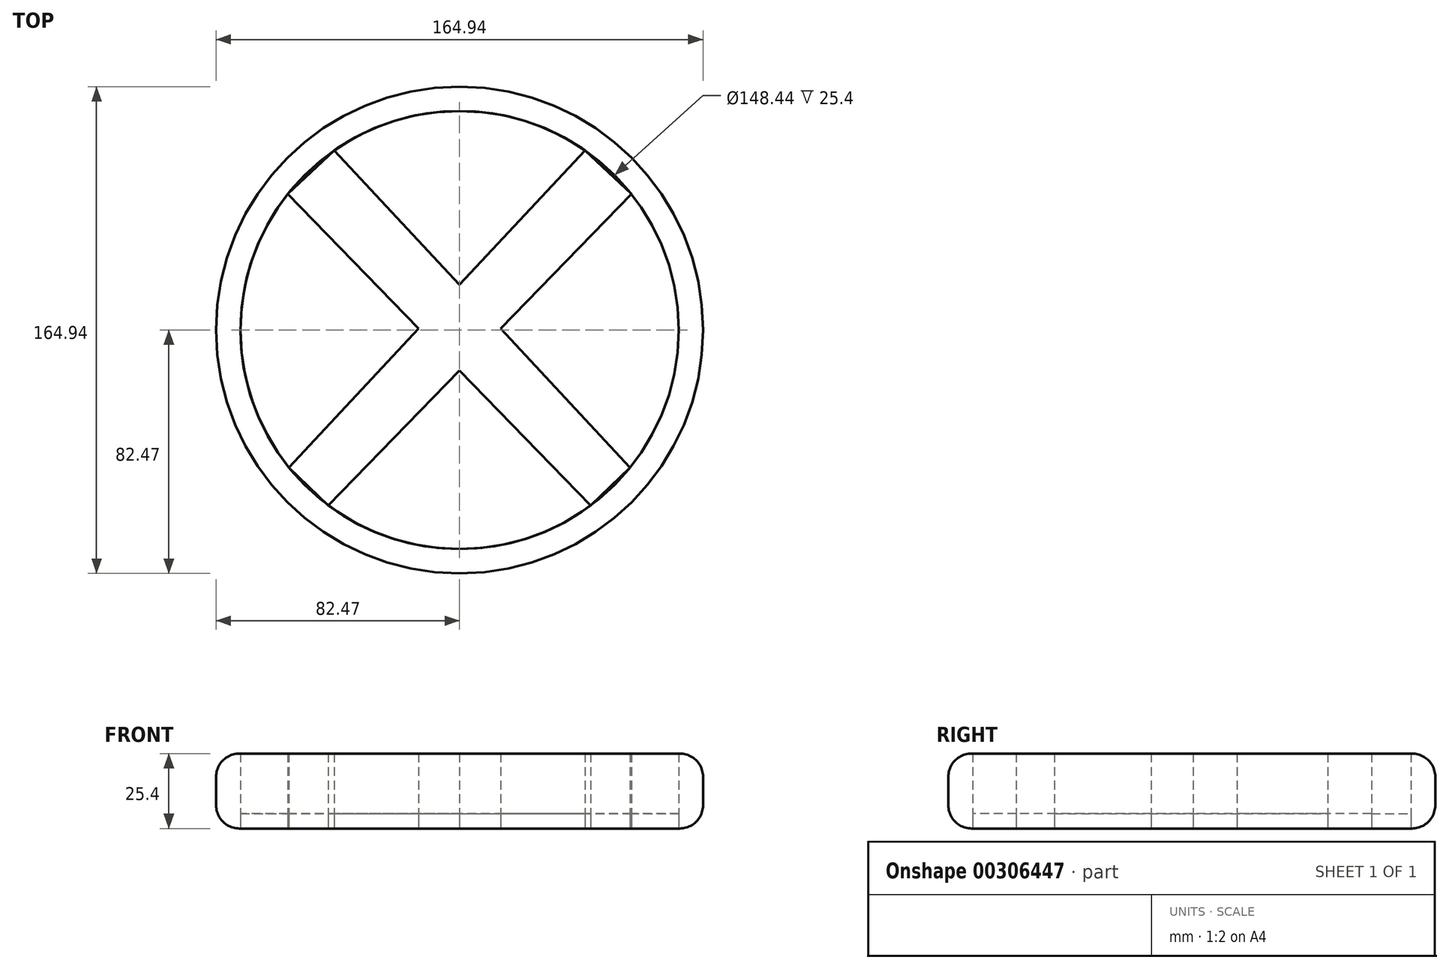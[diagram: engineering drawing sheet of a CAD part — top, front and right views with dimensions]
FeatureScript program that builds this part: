
annotation { "Feature Type Name" : "Feature", "Feature Type Description" : "" }
export const myFeature = defineFeature(function(context is Context, id is Id, definition is map)
    precondition{}
    {
        {
            var Q0;
            Q0=qCreatedBy(makeId("Top.planeOp"),FACE);
            var sketch = newSketch(context, id + "F0", { "sketchPlane" : qUnion([Q0])});
            skCircle(sketch, "E0", {"center": v(0, 0) * mm, "radius": 74.22 * mm});
            skLineSegment(sketch, "E1", {"start": v(-42.45, 60.88) * mm, "end": v(57.79, -46.57) * mm});
            skLineSegment(sketch, "E2", {"start": v(-58.2, 46.06) * mm, "end": v(44.46, -59.43) * mm});
            skLineSegment(sketch, "E3", {"start": v(44.46, -59.43) * mm, "end": v(57.79, -46.57) * mm});
            skLineSegment(sketch, "E4", {"start": v(-58.2, 46.06) * mm, "end": v(-42.45, 60.88) * mm});
            skLineSegment(sketch, "E5.MirrorCS", {"start": v(42.45, 60.88) * mm, "end": v(-57.79, -46.57) * mm});
            skLineSegment(sketch, "E6.MirrorCS", {"start": v(58.2, 46.06) * mm, "end": v(-44.46, -59.43) * mm});
            skLineSegment(sketch, "E7.MirrorCS", {"start": v(-44.46, -59.43) * mm, "end": v(-57.79, -46.57) * mm});
            skLineSegment(sketch, "E8.MirrorCS", {"start": v(58.2, 46.06) * mm, "end": v(42.45, 60.88) * mm});
            skCircle(sketch, "E9", {"center": v(0, 0) * mm, "radius": 82.47 * mm});
            skSolve(sketch);
        }
        {
            var Q0;
            {var subQ0=sQuery(id+"F0.wireOp",EDGE,"E4");Q0=makeQuery(id+"F0.imprint","IMPRINT",FACE,{"disambiguationData":[TD([[makeQuery(id+"F0.imprint","IMPRINT",EDGE,{"derivedFrom":subQ0}),-1.0]])]});}
            var Q1;
            {var subQ5=sQuery(id+"F0.wireOp",EDGE,"E8.MirrorCS");Q1=makeQuery(id+"F0.imprint","IMPRINT",FACE,{"disambiguationData":[TD([[makeQuery(id+"F0.imprint","IMPRINT",EDGE,{"derivedFrom":subQ5}),1.0]])]});}
            var Q2;
            {var subQ0=sQuery(id+"F0.wireOp",EDGE,"E5.MirrorCS");var subQ1=sQuery(id+"F0.wireOp",EDGE,"E1");var subQ2=makeQuery(id+"F0.imprint","INTERSECT",VERTEX,{"derivedFrom":[subQ1,subQ0]});Q2=makeQuery(id+"F0.imprint","IMPRINT",FACE,{"disambiguationData":[TD([[makeQuery(id+"F0.imprint","IMPRINT",EDGE,{"disambiguationData":[TD([[subQ2,-1.0]])],"derivedFrom":subQ1}),-1.0]])]});}
            var Q3;
            {var subQ5=sQuery(id+"F0.wireOp",EDGE,"E7.MirrorCS");Q3=makeQuery(id+"F0.imprint","IMPRINT",FACE,{"disambiguationData":[TD([[makeQuery(id+"F0.imprint","IMPRINT",EDGE,{"derivedFrom":subQ5}),-1.0]])]});}
            var Q4;
            {var subQ0=sQuery(id+"F0.wireOp",EDGE,"E3");Q4=makeQuery(id+"F0.imprint","IMPRINT",FACE,{"disambiguationData":[TD([[makeQuery(id+"F0.imprint","IMPRINT",EDGE,{"derivedFrom":subQ0}),1.0]])]});}
            var Q5;
            Q5=makeQuery(id+"F0.imprint","IMPRINT",FACE,{"disambiguationData":[TD([[makeQuery(id+"F0.imprint","IMPRINT",EDGE,{"derivedFrom":sQuery(id+"F0.wireOp",EDGE,"E9")}),1.0]])]});
            extrude(context, id + "F1", {"entities" : qUnion([Q0, Q1, Q2, Q3, Q4, Q5]), "depth" : 25.4 * mm});
        }
        {
            var Q0;
            {var subQ0=sQuery(id+"F0.wireOp",EDGE,"E2");var subQ3=sQuery(id+"F0.wireOp",EDGE,"E5.MirrorCS");var subQ5=makeQuery(id+"F0.imprint","INTERSECT",VERTEX,{"derivedFrom":[subQ0,subQ3]});Q0=makeQuery(id+"F0.imprint","IMPRINT",FACE,{"disambiguationData":[TD([[makeQuery(id+"F0.imprint","IMPRINT",EDGE,{"disambiguationData":[TD([[subQ5,1.0]])],"derivedFrom":subQ0}),-1.0]])]});}
            var Q1;
            {var subQ0=sQuery(id+"F0.wireOp",EDGE,"E1");var subQ3=sQuery(id+"F0.wireOp",EDGE,"E5.MirrorCS");var subQ5=makeQuery(id+"F0.imprint","INTERSECT",VERTEX,{"derivedFrom":[subQ0,subQ3]});Q1=makeQuery(id+"F0.imprint","IMPRINT",FACE,{"disambiguationData":[TD([[makeQuery(id+"F0.imprint","IMPRINT",EDGE,{"disambiguationData":[TD([[subQ5,1.0]])],"derivedFrom":subQ0}),1.0]])]});}
            var Q2;
            {var subQ0=sQuery(id+"F0.wireOp",EDGE,"E1");var subQ3=sQuery(id+"F0.wireOp",EDGE,"E6.MirrorCS");var subQ5=makeQuery(id+"F0.imprint","INTERSECT",VERTEX,{"derivedFrom":[subQ0,subQ3]});Q2=makeQuery(id+"F0.imprint","IMPRINT",FACE,{"disambiguationData":[TD([[makeQuery(id+"F0.imprint","IMPRINT",EDGE,{"disambiguationData":[TD([[subQ5,-1.0]])],"derivedFrom":subQ0}),1.0]])]});}
            var Q3;
            {var subQ0=sQuery(id+"F0.wireOp",EDGE,"E2");var subQ3=sQuery(id+"F0.wireOp",EDGE,"E6.MirrorCS");var subQ5=makeQuery(id+"F0.imprint","INTERSECT",VERTEX,{"derivedFrom":[subQ0,subQ3]});Q3=makeQuery(id+"F0.imprint","IMPRINT",FACE,{"disambiguationData":[TD([[makeQuery(id+"F0.imprint","IMPRINT",EDGE,{"disambiguationData":[TD([[subQ5,-1.0]])],"derivedFrom":subQ0}),-1.0]])]});}
            extrude(context, id + "F2", {"entities" : qUnion([Q0, Q1, Q2, Q3]), "depth" : 5.08 * mm});
        }
        {
            var Q0;
            Q0=makeQuery(id+"F1.opExtrude","CAP_EDGE",EDGE,{"disambiguationData":[OSD([sQuery(id+"F0.wireOp",EDGE,"E9")])],"isStart":false});
            var Q1;
            Q1=makeQuery(id+"F1.opExtrude","CAP_EDGE",EDGE,{"disambiguationData":[OSD([sQuery(id+"F0.wireOp",EDGE,"E9")])],"isStart":true});
            fillet(context, id + "F3", {"entities" : qUnion([Q0, Q1]), "radius" : 7.87 * mm, "tangentPropagation" : true, "allowEdgeOverflow" : false});
        }
    });
